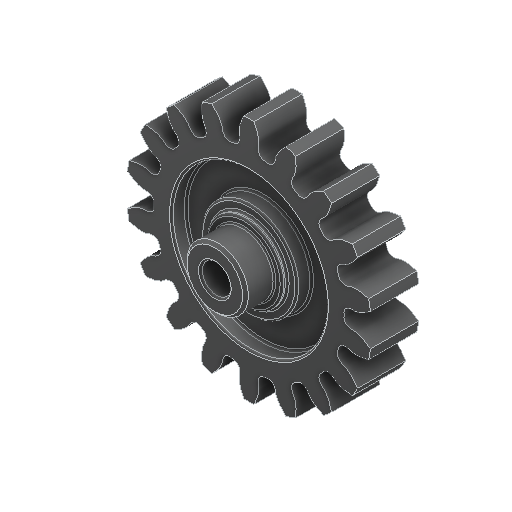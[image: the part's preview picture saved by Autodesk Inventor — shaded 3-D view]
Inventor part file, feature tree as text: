
AUTODESK INVENTOR PART (.ipt)
format: ipt  version: 2024.1 (Build 281209000, 209)  size: 429,056 bytes
history: native  units: in
note: dims shown in document units (in); Inventor stores cm internally (conversion verified against a paired STEP export)
features: chamfer x1
ambient origin geometry x8: Origin, YZ Plane, XZ Plane, XY Plane, X Axis, Y Axis, Z Axis, Center Point
bodies: Solid1 (feature_tree)
feature tree (1):
  chamfer  "Chamfer4"  [1 undecoded]
note: 1 required parameter value undecoded (feature->parameter linkage not recoverable at this tier; creation-order binding heuristic only, values carry confidence <= 0.55)
